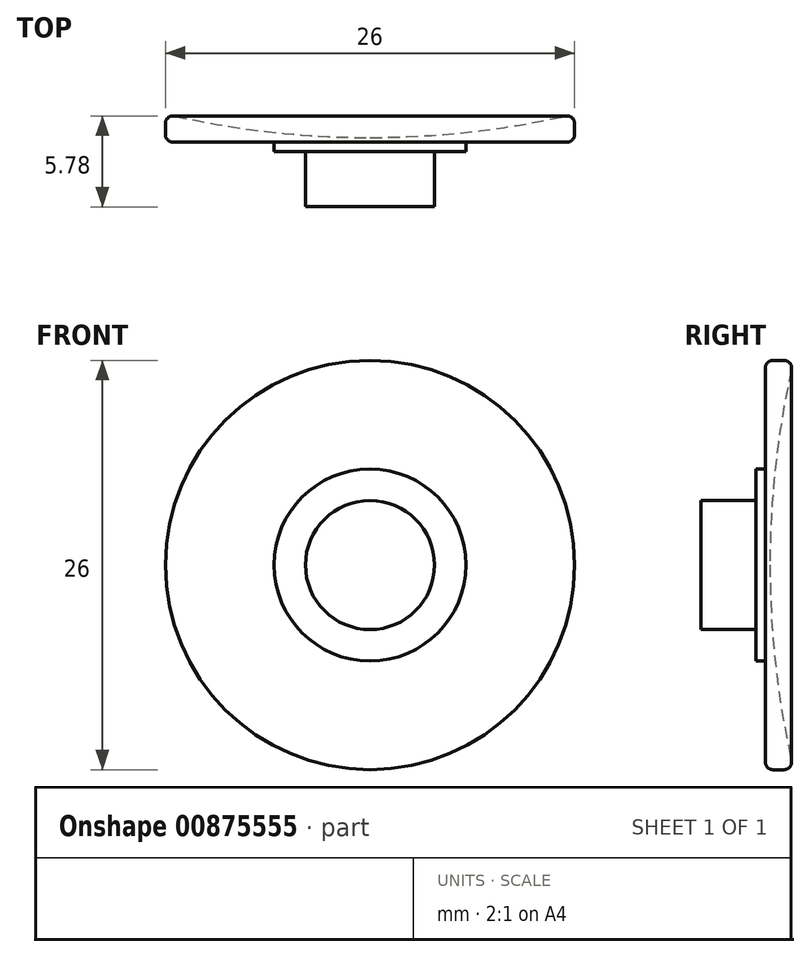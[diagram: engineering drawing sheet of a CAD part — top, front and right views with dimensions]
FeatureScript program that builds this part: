
annotation { "Feature Type Name" : "Feature", "Feature Type Description" : "" }
export const myFeature = defineFeature(function(context is Context, id is Id, definition is map)
    precondition{}
    {
        {
            var Q0;
            Q0=qCreatedBy(makeId("Top.planeOp"),FACE);
            var sketch = newSketch(context, id + "F0", { "sketchPlane" : qUnion([Q0])});
            skLineSegment(sketch, "E0", {"start": v(-13, 16.42) * mm, "end": v(-13, 14.62) * mm});
            skLineSegment(sketch, "E1", {"start": v(-13, 14.62) * mm, "end": v(-6.1, 14.62) * mm});
            skLineSegment(sketch, "E2", {"start": v(-6.1, 14.62) * mm, "end": v(-6.1, 14.02) * mm});
            skLineSegment(sketch, "E3", {"start": v(-6.1, 14.02) * mm, "end": v(-4.1, 14.02) * mm});
            skLineSegment(sketch, "E4", {"start": v(-4.1, 14.02) * mm, "end": v(-4.1, 10.52) * mm});
            skLineSegment(sketch, "E5", {"start": v(-4.1, 10.52) * mm, "end": v(0, 10.52) * mm});
            skLineSegment(sketch, "E6", {"start": v(0, 10.52) * mm, "end": v(0, 14.92) * mm});
            skLineSegment(sketch, "E7", {"start": v(-13, 16.42) * mm, "end": v(-13, 16.42) * mm});
            skLineSegment(sketch, "E8", {"start": v(-13, 16.42) * mm, "end": v(0, 16.42) * mm, "construction": true});
            skLineSegment(sketch, "E9.MirrorCS", {"start": v(13, 16.42) * mm, "end": v(13, 14.62) * mm, "construction": true});
            skArc(sketch, "E10", {"start": v(-13, 16.42) * mm, "mid": v(-6.54, 15.3) * mm, "end": v(0, 14.92) * mm});
            skArc(sketch, "E11", {"start": v(0, 14.92) * mm, "mid": v(6.54, 15.3) * mm, "end": v(13, 16.42) * mm, "construction": true});
            skSolve(sketch);
        }
        {
            var Q0;
            Q0=makeQuery(id+"F0.imprint","IMPRINT",FACE,{"disambiguationData":[TD([[makeQuery(id+"F0.imprint","IMPRINT",EDGE,{"derivedFrom":sQuery(id+"F0.wireOp",EDGE,"E0")}),1.0]])]});
            var Q1;
            Q1=sQuery(id+"F0.wireOp",EDGE,"E6");
            revolve(context, id + "F1", {"surfaceOperationType" : NewSurfaceOperationType.NEW, "entities" : qUnion([Q0]), "axis" : qUnion([Q1]), "revolveType" : RevolveType.FULL});
        }
        {
            var Q0;
            Q0=makeQuery(id+"F1.opRevolve","SWEPT_EDGE",EDGE,{"disambiguationData":[OSD([sQuery(id+"F0.wireOp",EDGE,"E0"),sQuery(id+"F0.wireOp",EDGE,"u05w0r4C-gUQf-vnxc-Hcyf-mIB32bVZgCP1")])]});
            var Q1;
            Q1=makeQuery(id+"F1.opRevolve","SWEPT_EDGE",EDGE,{"disambiguationData":[OSD([sQuery(id+"F0.wireOp",EDGE,"E0"),sQuery(id+"F0.wireOp",EDGE,"E1")])]});
            fillet(context, id + "F2", {"entities" : qUnion([Q0, Q1]), "radius" : .5 * mm, "tangentPropagation" : true, "allowEdgeOverflow" : false});
        }
    });
